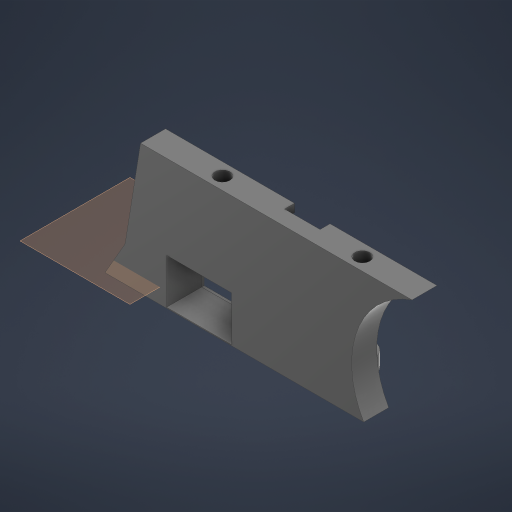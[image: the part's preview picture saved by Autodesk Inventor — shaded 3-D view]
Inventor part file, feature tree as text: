
AUTODESK INVENTOR PART (.ipt)
format: ipt  version: 2024 (Build 280153000, 153)  size: 300,544 bytes
history: native  units: in
note: dims shown in document units (in); Inventor stores cm internally (conversion verified against a paired STEP export)
features: extrude x7, sketch x7, chamfer x2, plane x1, fillet x1
ambient origin geometry x8: Origin, YZ Plane, XZ Plane, XY Plane, X Axis, Y Axis, Z Axis, Center Point
bodies: Solid1 (feature_tree)
feature tree (18):
  extrude  "Extrusion1"  Depth=0.315in
  plane  "Work Plane1"
  extrude  "Extrusion4"  Depth=0.1969in TaperAngle=0.0deg
  chamfer  "Chamfer2"  Distance=0.0984in Angle=45.0deg
  extrude  "Extrusion5"  Depth=0.5in
  extrude  "Extrusion6"  Depth=0.0787in TaperAngle=0.0deg
  chamfer  "Chamfer3"  Distance=0.0512in
  extrude  "Extrusion8"  Depth=0.1181in TaperAngle=0.0deg
  extrude  "Extrusion9"  Depth=0.0787in TaperAngle=0.0deg
  extrude  "Extrusion10"  [1 undecoded]
  fillet  "Fillet3"  [1 undecoded]
  sketch  "Sketch1"  dims[d1=0.1969in d2=0.0in d31=0.315in]
  sketch  "Sketch4"  dims[d32=0.1575in d33=0.1969in d34=0.0in d35=0.0984in d36=0.1772in d37=45.0deg]
  sketch  "Sketch6"  dims[d39=0.5in d41=0.5in]
  sketch  "Sketch7"  dims[d42=0.25in d43=0.0787in d44=0.0in d45=0.0512in d46=0.0in]
  sketch  "Sketch9"  dims[d47=0.315in d48=0.0787in d49=0.1374in d58=0.1181in d59=0.0in]
  sketch  "Sketch10"  dims[d60=0.0787in d61=0.0in d62=0.0787in d63=0.0in]
  sketch  "Sketch11"  dims[d64=0.1181in]
note: 2 required parameter values undecoded (feature->parameter linkage not recoverable at this tier; creation-order binding heuristic only, values carry confidence <= 0.55)
